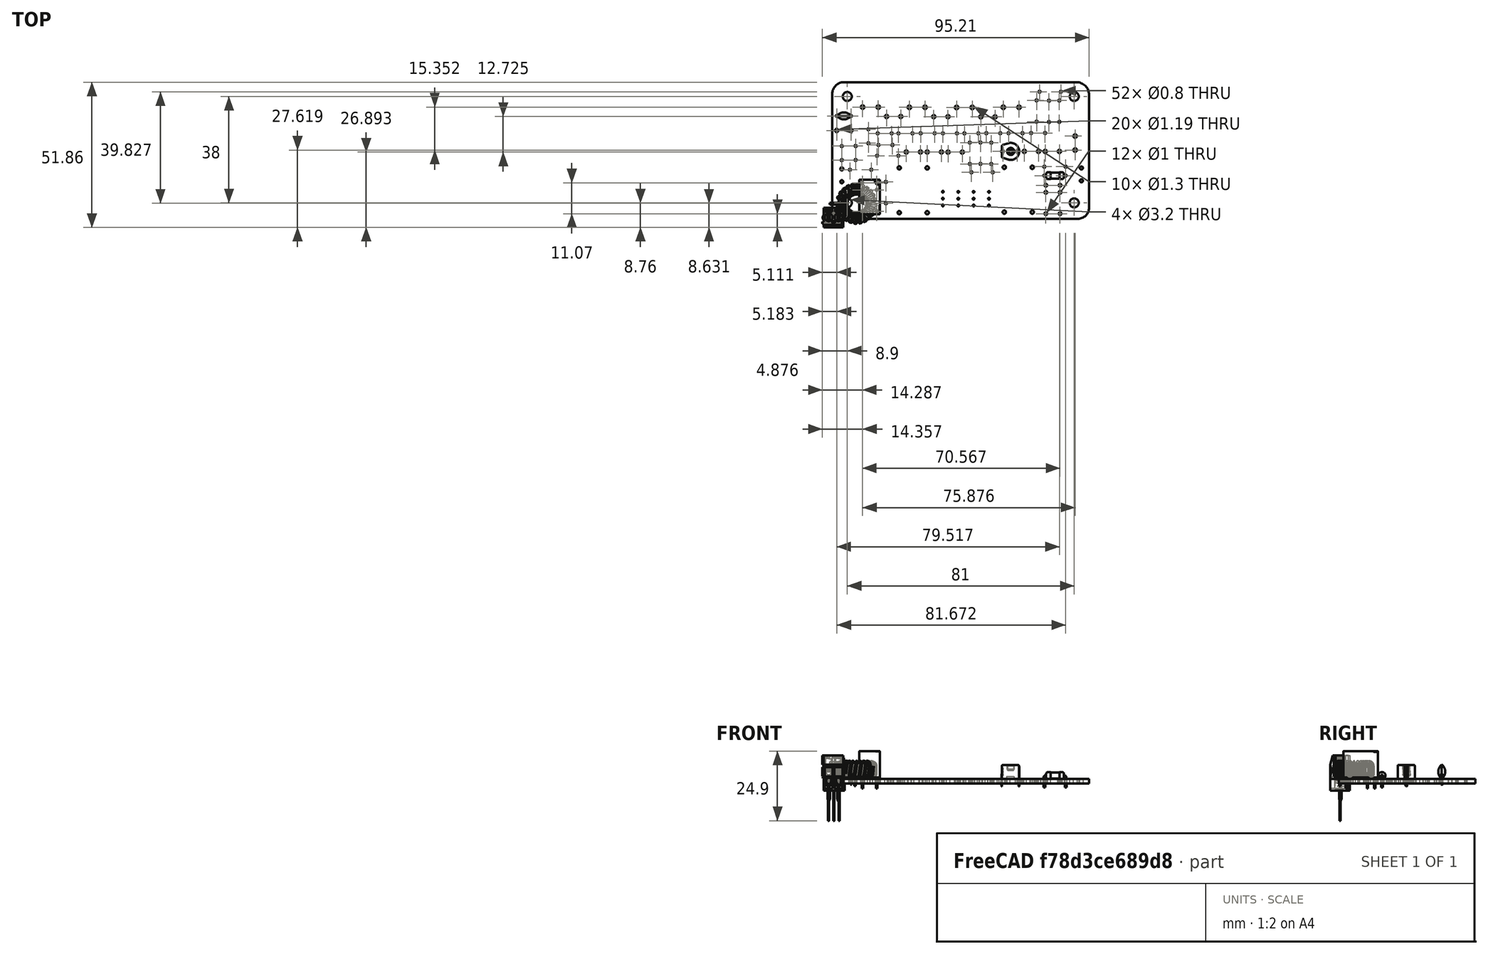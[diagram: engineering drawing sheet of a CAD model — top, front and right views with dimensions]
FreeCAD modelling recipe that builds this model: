
FCSTD DOCUMENT  (FreeCAD 0.19R24267 +148 (Git))
Label: resolution-filters
License: All rights reserved
LicenseURL: http://en.wikipedia.org/wiki/All_rights_reserved
objects: App::Link×60, Part::Feature×41, App::Part×10, PartDesign::CoordinateSystem×1, Sketcher::SketchObject×1
note: 43 computed .brp shape members not serialized (recipe doc carries the construction recipe); baked Part::Feature solids carry a one-line shape summary decoded from their .brp

FEATURE [PartDesign::CoordinateSystem] Local_CS_9a4e
  AttacherType = Attacher::AttachEngine3D
FEATURE [Part::Feature] Pcb_9a4e
  Placement = pos=(-101.6,111.76,0) rot=(0,0,1;0rad)
  shape: bbox 91.69 x 48.77 x 1.6 mm, 132 faces (baked)
FEATURE [Sketcher::SketchObject] PCB_Sketch_9a4e
  FullyConstrained = false
  sketch-geometry (8):
    g0: LineSegment StartX=86.7015 StartY=48.3617 StartZ=0 EndX=3.72385 EndY=48.3617 EndZ=0
    g1: LineSegment StartX=91.2113 StartY=3.58242 StartZ=0 EndX=91.2113 EndY=43.852 EndZ=0
    g2: LineSegment StartX=-0.482737 StartY=44.1551 StartZ=0 EndX=-0.482737 EndY=4.1461 EndZ=0
    g3: LineSegment StartX=4.06962 StartY=-0.40626 StartZ=0 EndX=87.2226 EndY=-0.40626 EndZ=0
    g4: ArcOfCircle CenterX=3.72386 CenterY=44.1551 CenterZ=0 NormalX=0 NormalY=0 NormalZ=-1 AngleXU=2.45258e-06 Radius=4.2066 StartAngle=0 EndAngle=1.57079
    g5: ArcOfCircle CenterX=4.06966 CenterY=4.14614 CenterZ=0 NormalX=0 NormalY=0 NormalZ=-1 AngleXU=-1.57079 Radius=4.5524 StartAngle=0 EndAngle=1.57078
    g6: ArcOfCircle CenterX=87.2226 CenterY=3.58243 CenterZ=0 NormalX=0 NormalY=0 NormalZ=-1 AngleXU=-3.14159 Radius=3.98869 StartAngle=0 EndAngle=1.57079
    g7: ArcOfCircle CenterX=86.7014 CenterY=43.8519 CenterZ=0 NormalX=0 NormalY=0 NormalZ=-1 AngleXU=1.5708 Radius=4.50982 StartAngle=0 EndAngle=1.57078
  constraints (8):
    c: Coincident(g2,g5)
    c: Coincident(g2,g4)
    c: Coincident(g0,g4)
    c: Coincident(g3,g5)
    c: Coincident(g0,g7)
    c: Coincident(g3,g6)
    c: Coincident(g1,g6)
    c: Coincident(g1,g7)
FEATURE [Part::Feature] Shape  label="C513_Trimmer Cap - Brown_fa101f9de910"
  Placement = pos=(60.4359,23.6475,0) rot=(0,0,1;0rad)
  shape: bbox 6.858 x 6.618 x 7.625 mm, 264 faces (baked)
FEATURE [App::Link] C513_Trimmer_Cap___Brown_fa101f9de910_ln_  label="C513_Trimmer Cap - Brown_fa101f9de910[2]"
  LinkPlacement = pos=(60.4359,23.6475,0) rot=(0,0,1;0rad)
  LinkedObject = -> Shape
  Placement = pos=(60.4359,23.6475,0) rot=(0,0,1;0rad)
FEATURE [App::Link] C513_Trimmer_Cap___Brown_fa101f9de910_ln_001  label="C510_Trimmer Cap - Brown_b6d9ad9018ce"
  LinkPlacement = pos=(18.9169,36.1188,0) rot=(0,0,1;0rad)
  LinkedObject = -> Shape
  Placement = pos=(18.9169,36.1188,0) rot=(0,0,1;0rad)
FEATURE [App::Link] C513_Trimmer_Cap___Brown_fa101f9de910_ln_002  label="C510_Trimmer Cap - Brown_b6d9ad9018ce[2]"
  LinkPlacement = pos=(18.9169,36.1188,0) rot=(0,0,1;0rad)
  LinkedObject = -> Shape
  Placement = pos=(18.9169,36.1188,0) rot=(0,0,1;0rad)
FEATURE [Part::Feature] Part__Feature  label="T37-6 IND"
  Placement = pos=(0,-2.7,-0.5) rot=(1,0,0;1.5708rad)
  shape: bbox 10.32 x 3.252 x 10.32 mm, 8 faces, 0 solids (baked)
FEATURE [Part::Feature] Part__Feature001  label="T37-6 IND001"
  Placement = pos=(0,-2.7,-0.5) rot=(1,0,0;1.5708rad)
  shape: bbox 10.51 x 3.773 x 9.618 mm, 81 faces, 0 solids (baked)
FEATURE [Part::Feature] Part__Feature002  label="T37-6 IND002"
  Placement = pos=(0,-2.7,-0.5) rot=(1,0,0;1.5708rad)
  shape: bbox 2.23 x 4.584 x 1.894 mm, 1 faces, 0 solids (baked)
FEATURE [Part::Feature] Part__Feature003  label="T37-6 IND003"
  Placement = pos=(0,-2.7,-0.5) rot=(1,0,0;1.5708rad)
  shape: bbox 1.873 x 4.219 x 1.831 mm, 1 faces, 0 solids (baked)
FEATURE [App::Part] T37_6_IND004  label="L501_T37-6 IND004_9cd36dea0652"
  Group = -> [Part__Feature,Part__Feature001,Part__Feature002,Part__Feature003]
  Origin = -> Origin008
  Placement = pos=(15.9572,39.4716,0) rot=(0,0,-1;1.5708rad)
FEATURE [App::Link] L501_T37_6_IND004_9cd36dea0652_ln_  label="L501_T37-6 IND004_9cd36dea0652[2]"
  LinkPlacement = pos=(15.9572,39.4716,0) rot=(0,0,-1;1.5708rad)
  LinkedObject = -> T37_6_IND004
  Placement = pos=(15.9572,39.4716,0) rot=(0,0,-1;1.5708rad)
FEATURE [Part::Feature] Shape001  label="R509_R_Axial_DIN0207_L63mm_D25mm_P762mm_Horizontal_29629d9bf234"
  Placement = pos=(75.2348,14.986,0) rot=(0,0,1;0rad)
  shape: bbox 8.418 x 2.706 x 5.603 mm, 15 faces (baked)
FEATURE [App::Link] R509_R_Axial_DIN0207_L63mm_D25mm_P762mm_Horizontal_29629d9bf234_ln_  label="R501_R_Axial_DIN0207_L63mm_D25mm_P762mm_Horizontal_7b32fe088733"
  LinkPlacement = pos=(13.4366,17.0942,0) rot=(0,0,1;3.14159rad)
  LinkedObject = -> Shape001
  Placement = pos=(13.4366,17.0942,0) rot=(0,0,1;3.14159rad)
FEATURE [App::Link] C513_Trimmer_Cap___Brown_fa101f9de910_ln_003  label="C516_Trimmer Cap - Brown_1af99d41cc4e"
  LinkPlacement = pos=(68.0875,23.6475,0) rot=(0,0,1;0rad)
  LinkedObject = -> Shape
  Placement = pos=(68.0875,23.6475,0) rot=(0,0,1;0rad)
FEATURE [App::Link] C513_Trimmer_Cap___Brown_fa101f9de910_ln_004  label="C516_Trimmer Cap - Brown_1af99d41cc4e[2]"
  LinkPlacement = pos=(68.0875,23.6475,0) rot=(0,0,1;0rad)
  LinkedObject = -> Shape
  Placement = pos=(68.0875,23.6475,0) rot=(0,0,1;0rad)
FEATURE [App::Link] C513_Trimmer_Cap___Brown_fa101f9de910_ln_005  label="C508_Trimmer Cap - Brown_be8f6a1adee0"
  LinkPlacement = pos=(33.4203,23.4188,0) rot=(0,0,1;0rad)
  LinkedObject = -> Shape
  Placement = pos=(33.4203,23.4188,0) rot=(0,0,1;0rad)
FEATURE [App::Link] C513_Trimmer_Cap___Brown_fa101f9de910_ln_006  label="C508_Trimmer Cap - Brown_be8f6a1adee0[2]"
  LinkPlacement = pos=(33.4203,23.4188,0) rot=(0,0,1;0rad)
  LinkedObject = -> Shape
  Placement = pos=(33.4203,23.4188,0) rot=(0,0,1;0rad)
FEATURE [App::Link] R509_R_Axial_DIN0207_L63mm_D25mm_P762mm_Horizontal_29629d9bf234_ln_001  label="R504_R_Axial_DIN0207_L63mm_D25mm_P762mm_Horizontal_66a026bb1076"
  LinkPlacement = pos=(73.533,44.958,0) rot=(0,0,1;0rad)
  LinkedObject = -> Shape001
  Placement = pos=(73.533,44.958,0) rot=(0,0,1;0rad)
FEATURE [App::Link] L501_T37_6_IND004_9cd36dea0652_ln_001  label="L503_T37-6 IND004_f84a305ee8ab"
  LinkPlacement = pos=(43.9106,39.3446,0) rot=(0,0,1;1.5708rad)
  LinkedObject = -> T37_6_IND004
  Placement = pos=(43.9106,39.3446,0) rot=(0,0,1;1.5708rad)
FEATURE [App::Link] L501_T37_6_IND004_9cd36dea0652_ln_002  label="L503_T37-6 IND004_f84a305ee8ab[2]"
  LinkPlacement = pos=(43.9106,39.3446,0) rot=(0,0,1;1.5708rad)
  LinkedObject = -> T37_6_IND004
  Placement = pos=(43.9106,39.3446,0) rot=(0,0,1;1.5708rad)
FEATURE [Part::Feature] Shape002  label="C506_C_Disc_D50mm_W25mm_P500mm_f2b36a464e24"
  Placement = pos=(1.183,36.322,0) rot=(0,0,1;0rad)
  shape: bbox 5.5 x 2.5 x 7.1 mm, 10 faces (baked)
FEATURE [App::Link] C513_Trimmer_Cap___Brown_fa101f9de910_ln_007  label="C520_Trimmer Cap - Brown_a66b8da15489"
  LinkPlacement = pos=(52.5719,35.9918,0) rot=(0,0,1;0rad)
  LinkedObject = -> Shape
  Placement = pos=(52.5719,35.9918,0) rot=(0,0,1;0rad)
FEATURE [App::Link] C513_Trimmer_Cap___Brown_fa101f9de910_ln_008  label="C520_Trimmer Cap - Brown_a66b8da15489[2]"
  LinkPlacement = pos=(52.5719,35.9918,0) rot=(0,0,1;0rad)
  LinkedObject = -> Shape
  Placement = pos=(52.5719,35.9918,0) rot=(0,0,1;0rad)
FEATURE [App::Link] R509_R_Axial_DIN0207_L63mm_D25mm_P762mm_Horizontal_29629d9bf234_ln_002  label="R503_R_Axial_DIN0207_L63mm_D25mm_P762mm_Horizontal_265a809a3c5d"
  LinkPlacement = pos=(18.669,12.7508,0) rot=(0,0,-1;1.5708rad)
  LinkedObject = -> Shape001
  Placement = pos=(18.669,12.7508,0) rot=(0,0,-1;1.5708rad)
FEATURE [App::Link] C513_Trimmer_Cap___Brown_fa101f9de910_ln_009  label="C515_Trimmer Cap - Brown_f30af8ea2418"
  LinkPlacement = pos=(35.7571,36.0426,0) rot=(0,0,1;0rad)
  LinkedObject = -> Shape
  Placement = pos=(35.7571,36.0426,0) rot=(0,0,1;0rad)
FEATURE [App::Link] C513_Trimmer_Cap___Brown_fa101f9de910_ln_010  label="C515_Trimmer Cap - Brown_f30af8ea2418[2]"
  LinkPlacement = pos=(35.7571,36.0426,0) rot=(0,0,1;0rad)
  LinkedObject = -> Shape
  Placement = pos=(35.7571,36.0426,0) rot=(0,0,1;0rad)
FEATURE [App::Link] L501_T37_6_IND004_9cd36dea0652_ln_003  label="L502_T37-6 IND004_d7aca97a7b04"
  LinkPlacement = pos=(27.045,39.3954,0) rot=(0,0,1;1.5708rad)
  LinkedObject = -> T37_6_IND004
  Placement = pos=(27.045,39.3954,0) rot=(0,0,1;1.5708rad)
FEATURE [App::Link] L501_T37_6_IND004_9cd36dea0652_ln_004  label="L502_T37-6 IND004_d7aca97a7b04[2]"
  LinkPlacement = pos=(27.045,39.3954,0) rot=(0,0,1;1.5708rad)
  LinkedObject = -> T37_6_IND004
  Placement = pos=(27.045,39.3954,0) rot=(0,0,1;1.5708rad)
FEATURE [App::Link] C506_C_Disc_D50mm_W25mm_P500mm_f2b36a464e24_ln_  label="C524_C_Disc_D50mm_W25mm_P500mm_c3d2106afa5c"
  LinkPlacement = pos=(62.4478,30.1498,0) rot=(0,0,1;0rad)
  LinkedObject = -> Shape002
  Placement = pos=(62.4478,30.1498,0) rot=(0,0,1;0rad)
FEATURE [App::Link] C506_C_Disc_D50mm_W25mm_P500mm_f2b36a464e24_ln_001  label="C521_C_Disc_D50mm_W25mm_P500mm_ee262ac6dc63"
  LinkPlacement = pos=(75.5142,30.2006,0) rot=(0,0,1;3.14159rad)
  LinkedObject = -> Shape002
  Placement = pos=(75.5142,30.2006,0) rot=(0,0,1;3.14159rad)
FEATURE [Part::Feature] Part__Feature004  label="UM-1"
  Placement = pos=(0.1,2e-15,0.6) rot=(1,0,0;1.5708rad)
  shape: bbox 8 x 3.2 x 7.5 mm, 36 faces (baked)
FEATURE [Part::Feature] Part__Feature005  label="UM-002"
  Placement = pos=(0.1,2e-15,0.6) rot=(1,0,0;1.5708rad)
  shape: bbox 1.2 x 1.2 x 0.5 mm, 6 faces (baked)
FEATURE [Part::Feature] Part__Feature006  label="UM-003"
  Placement = pos=(0.1,2e-15,0.6) rot=(1,0,0;1.5708rad)
  shape: bbox 1.2 x 1.2 x 0.5 mm, 6 faces (baked)
FEATURE [Part::Feature] Part__Feature007  label="UM-004"
  Placement = pos=(0.1,2e-15,0.6) rot=(1,0,0;1.5708rad)
  shape: bbox 0.35 x 0.35 x 15.5 mm, 4 faces (baked)
FEATURE [Part::Feature] Part__Feature008  label="UM-005"
  Placement = pos=(0.1,2e-15,0.6) rot=(1,0,0;1.5708rad)
  shape: bbox 0.35 x 0.35 x 15.5 mm, 4 faces (baked)
FEATURE [Part::Feature] Part__Feature009  label="UM-006"
  Placement = pos=(0.1,2e-15,0.6) rot=(1,0,0;1.5708rad)
  shape: bbox 0.35 x 0.35 x 15.5 mm, 4 faces (baked)
FEATURE [App::Part] UM_007  label="Y503_UM-007_13096f2298e0"
  Group = -> [Part__Feature004,Part__Feature005,Part__Feature006,Part__Feature007,Part__Feature008,Part__Feature009]
  Origin = -> Origin009
  Placement = pos=(49.9872,6.7641,0) rot=(0,0,1;1.5708rad)
FEATURE [App::Link] Y503_UM_007_13096f2298e0_ln_  label="Y503_UM-007_13096f2298e0[2]"
  LinkPlacement = pos=(49.9872,6.7641,0) rot=(0,0,1;1.5708rad)
  LinkedObject = -> UM_007
  Placement = pos=(49.9872,6.7641,0) rot=(0,0,1;1.5708rad)
FEATURE [App::Link] R509_R_Axial_DIN0207_L63mm_D25mm_P762mm_Horizontal_29629d9bf234_ln_003  label="R511_R_Axial_DIN0207_L63mm_D25mm_P762mm_Horizontal_370c389b173b"
  LinkPlacement = pos=(49.1744,16.1798,0) rot=(0,0,1;0rad)
  LinkedObject = -> Shape001
  Placement = pos=(49.1744,16.1798,0) rot=(0,0,1;0rad)
FEATURE [App::Link] R509_R_Axial_DIN0207_L63mm_D25mm_P762mm_Horizontal_29629d9bf234_ln_004  label="R506_R_Axial_DIN0207_L63mm_D25mm_P762mm_Horizontal_386c48cb915c"
  LinkPlacement = pos=(48.641,26.797,0) rot=(0,0,-1;1.5708rad)
  LinkedObject = -> Shape001
  Placement = pos=(48.641,26.797,0) rot=(0,0,-1;1.5708rad)
FEATURE [App::Link] R509_R_Axial_DIN0207_L63mm_D25mm_P762mm_Horizontal_29629d9bf234_ln_005  label="R502_R_Axial_DIN0207_L63mm_D25mm_P762mm_Horizontal_210b6273bd98"
  LinkPlacement = pos=(15.5194,22.098,0) rot=(0,0,1;0rad)
  LinkedObject = -> Shape001
  Placement = pos=(15.5194,22.098,0) rot=(0,0,1;0rad)
FEATURE [App::Link] C506_C_Disc_D50mm_W25mm_P500mm_f2b36a464e24_ln_002  label="C522_C_Disc_D50mm_W25mm_P500mm_f3233de2541f"
  LinkPlacement = pos=(46.6998,30.099,0) rot=(0,0,1;0rad)
  LinkedObject = -> Shape002
  Placement = pos=(46.6998,30.099,0) rot=(0,0,1;0rad)
FEATURE [Part::Feature] Part__Feature010  label="L_Tor_13x8x5_3a_cp"
  shape: bbox 14.07 x 14.07 x 5 mm, 8 faces (baked)
FEATURE [Part::Feature] Part__Feature011  label="L_Tor_13x8x5_3a_cp001"
  shape: bbox 16.93 x 14.67 x 6.694 mm, 203 faces (baked)
FEATURE [App::Part] L_Tor_13x8x5_3a_cp  label="T501_L_Tor_13x8x5_3a_cp002_fb5841712b66"
  Group = -> [Part__Feature010,Part__Feature011]
  Origin = -> Origin010
  Placement = pos=(23.4188,17.7546,0) rot=(0,0,-1;1.5708rad)
FEATURE [App::Link] T501_L_Tor_13x8x5_3a_cp002_fb5841712b66_ln_  label="T501_L_Tor_13x8x5_3a_cp002_fb5841712b66[2]"
  LinkPlacement = pos=(23.4188,17.7546,0) rot=(0,0,-1;1.5708rad)
  LinkedObject = -> L_Tor_13x8x5_3a_cp
  Placement = pos=(23.4188,17.7546,0) rot=(0,0,-1;1.5708rad)
FEATURE [App::Link] C513_Trimmer_Cap___Brown_fa101f9de910_ln_011  label="C505_Trimmer Cap - Brown_67148adb1c4f"
  LinkPlacement = pos=(25.9527,23.4442,0) rot=(0,0,1;0rad)
  LinkedObject = -> Shape
  Placement = pos=(25.9527,23.4442,0) rot=(0,0,1;0rad)
FEATURE [App::Link] C513_Trimmer_Cap___Brown_fa101f9de910_ln_012  label="C505_Trimmer Cap - Brown_67148adb1c4f[2]"
  LinkPlacement = pos=(25.9527,23.4442,0) rot=(0,0,1;0rad)
  LinkedObject = -> Shape
  Placement = pos=(25.9527,23.4442,0) rot=(0,0,1;0rad)
FEATURE [App::Link] C506_C_Disc_D50mm_W25mm_P500mm_f2b36a464e24_ln_003  label="C509_C_Disc_D50mm_W25mm_P500mm_400302d33418"
  LinkPlacement = pos=(15.7518,30.0991,0) rot=(0,0,1;0rad)
  LinkedObject = -> Shape002
  Placement = pos=(15.7518,30.0991,0) rot=(0,0,1;0rad)
FEATURE [App::Link] C506_C_Disc_D50mm_W25mm_P500mm_f2b36a464e24_ln_004  label="C514_C_Disc_D50mm_W25mm_P500mm_138143d8e988"
  LinkPlacement = pos=(23.1587,30.0991,0) rot=(0,0,1;0rad)
  LinkedObject = -> Shape002
  Placement = pos=(23.1587,30.0991,0) rot=(0,0,1;0rad)
FEATURE [App::Link] C506_C_Disc_D50mm_W25mm_P500mm_f2b36a464e24_ln_005  label="C507_C_Disc_D50mm_W25mm_P500mm_249115c39c3e"
  LinkPlacement = pos=(12.4206,31.5576,0) rot=(0,0,-1;1.5708rad)
  LinkedObject = -> Shape002
  Placement = pos=(12.4206,31.5576,0) rot=(0,0,-1;1.5708rad)
FEATURE [App::Link] C506_C_Disc_D50mm_W25mm_P500mm_f2b36a464e24_ln_006  label="C512_C_Disc_D50mm_W25mm_P500mm_561b1da62fe1"
  LinkPlacement = pos=(16.0166,25.9334,0) rot=(0,0,1;0rad)
  LinkedObject = -> Shape002
  Placement = pos=(16.0166,25.9334,0) rot=(0,0,1;0rad)
FEATURE [App::Link] Y503_UM_007_13096f2298e0_ln_001  label="Y504_UM-007_ad74b97e0cd8"
  LinkPlacement = pos=(55.4736,6.7641,0) rot=(0,0,1;1.5708rad)
  LinkedObject = -> UM_007
  Placement = pos=(55.4736,6.7641,0) rot=(0,0,1;1.5708rad)
FEATURE [App::Link] Y503_UM_007_13096f2298e0_ln_002  label="Y504_UM-007_ad74b97e0cd8[2]"
  LinkPlacement = pos=(55.4736,6.7641,0) rot=(0,0,1;1.5708rad)
  LinkedObject = -> UM_007
  Placement = pos=(55.4736,6.7641,0) rot=(0,0,1;1.5708rad)
FEATURE [App::Link] C506_C_Disc_D50mm_W25mm_P500mm_f2b36a464e24_ln_007  label="C517_C_Disc_D50mm_W25mm_P500mm_4a230a44a26d"
  LinkPlacement = pos=(31.0934,30.1244,0) rot=(0,0,1;0rad)
  LinkedObject = -> Shape002
  Placement = pos=(31.0934,30.1244,0) rot=(0,0,1;0rad)
FEATURE [App::Link] R509_R_Axial_DIN0207_L63mm_D25mm_P762mm_Horizontal_29629d9bf234_ln_006  label="R507_R_Axial_DIN0207_L63mm_D25mm_P762mm_Horizontal_1a8086ba3037"
  LinkPlacement = pos=(56.2864,19.1516,0) rot=(0,0,1;1.5708rad)
  LinkedObject = -> Shape001
  Placement = pos=(56.2864,19.1516,0) rot=(0,0,1;1.5708rad)
FEATURE [App::Link] C506_C_Disc_D50mm_W25mm_P500mm_f2b36a464e24_ln_008  label="C501_C_Disc_D50mm_W25mm_P500mm_c7547f0456a5"
  LinkPlacement = pos=(7.874,25.574,0) rot=(0,0,-1;1.5708rad)
  LinkedObject = -> Shape002
  Placement = pos=(7.874,25.574,0) rot=(0,0,-1;1.5708rad)
FEATURE [App::Link] T501_L_Tor_13x8x5_3a_cp002_fb5841712b66_ln_001  label="T502_L_Tor_13x8x5_3a_cp002_44b5b7291388"
  LinkPlacement = pos=(70.9384,1.9568,0) rot=(0,0,1;1.5708rad)
  LinkedObject = -> L_Tor_13x8x5_3a_cp
  Placement = pos=(70.9384,1.9568,0) rot=(0,0,1;1.5708rad)
FEATURE [App::Link] T501_L_Tor_13x8x5_3a_cp002_fb5841712b66_ln_002  label="T502_L_Tor_13x8x5_3a_cp002_44b5b7291388[2]"
  LinkPlacement = pos=(70.9384,1.9568,0) rot=(0,0,1;1.5708rad)
  LinkedObject = -> L_Tor_13x8x5_3a_cp
  Placement = pos=(70.9384,1.9568,0) rot=(0,0,1;1.5708rad)
FEATURE [App::Link] Y503_UM_007_13096f2298e0_ln_003  label="Y501_UM-007_785145fc44e6"
  LinkPlacement = pos=(39.0144,6.7895,0) rot=(0,0,1;1.5708rad)
  LinkedObject = -> UM_007
  Placement = pos=(39.0144,6.7895,0) rot=(0,0,1;1.5708rad)
FEATURE [App::Link] Y503_UM_007_13096f2298e0_ln_004  label="Y501_UM-007_785145fc44e6[2]"
  LinkPlacement = pos=(39.0144,6.7895,0) rot=(0,0,1;1.5708rad)
  LinkedObject = -> UM_007
  Placement = pos=(39.0144,6.7895,0) rot=(0,0,1;1.5708rad)
FEATURE [App::Link] R509_R_Axial_DIN0207_L63mm_D25mm_P762mm_Horizontal_29629d9bf234_ln_007  label="R510_R_Axial_DIN0207_L63mm_D25mm_P762mm_Horizontal_af9739584a69"
  LinkPlacement = pos=(75.2348,18.1864,0) rot=(0,0,1;0rad)
  LinkedObject = -> Shape001
  Placement = pos=(75.2348,18.1864,0) rot=(0,0,1;0rad)
FEATURE [App::Link] C506_C_Disc_D50mm_W25mm_P500mm_f2b36a464e24_ln_009  label="C523_C_Disc_D50mm_W25mm_P500mm_b693a0d0fd5f"
  LinkPlacement = pos=(54.5122,30.1498,0) rot=(0,0,1;0rad)
  LinkedObject = -> Shape002
  Placement = pos=(54.5122,30.1498,0) rot=(0,0,1;0rad)
FEATURE [App::Link] C506_C_Disc_D50mm_W25mm_P500mm_f2b36a464e24_ln_010  label="C519_C_Disc_D50mm_W25mm_P500mm_4a3058133605"
  LinkPlacement = pos=(39.0337,30.0991,0) rot=(0,0,1;0rad)
  LinkedObject = -> Shape002
  Placement = pos=(39.0337,30.0991,0) rot=(0,0,1;0rad)
FEATURE [Part::Feature] Part__Feature012  label="D_DO-35_SOD27_P7.62mm_Horizontal"
  shape: bbox 8.244 x 0.5 x 4.312 mm, 7 faces (baked)
FEATURE [Part::Feature] Part__Feature013  label="D_DO-35_SOD27_P7.62mm_Horizontal001"
  shape: bbox 4 x 2.165 x 2.165 mm, 9 faces (baked)
FEATURE [App::Part] D_DO_35_SOD27_P7_62mm_Horizontal  label="D501_D_DO-35_SOD27_P7.62mm_Horizontal002_73c7e2338286"
  Group = -> [Part__Feature012,Part__Feature013]
  Origin = -> Origin011
  Placement = pos=(72.4916,41.8846,0) rot=(0,0,-1;1.5708rad)
FEATURE [Part::Feature] Shape003  label="K501_Relay_SPDT_Omron_G5V-1_adee48805411"
  Placement = pos=(10.287,12.446,0) rot=(0,0,1;0rad)
  shape: bbox 7.3 x 12.3 x 13.4 mm, 63 faces (baked)
FEATURE [App::Link] C513_Trimmer_Cap___Brown_fa101f9de910_ln_013  label="C511_Trimmer Cap - Brown_927071e8bfa3"
  LinkPlacement = pos=(40.8686,23.3934,0) rot=(0,0,1;0rad)
  LinkedObject = -> Shape
  Placement = pos=(40.8686,23.3934,0) rot=(0,0,1;0rad)
FEATURE [App::Link] C513_Trimmer_Cap___Brown_fa101f9de910_ln_014  label="C511_Trimmer Cap - Brown_927071e8bfa3[2]"
  LinkPlacement = pos=(40.8686,23.3934,0) rot=(0,0,1;0rad)
  LinkedObject = -> Shape
  Placement = pos=(40.8686,23.3934,0) rot=(0,0,1;0rad)
FEATURE [App::Link] R509_R_Axial_DIN0207_L63mm_D25mm_P762mm_Horizontal_29629d9bf234_ln_008  label="R505_R_Axial_DIN0207_L63mm_D25mm_P762mm_Horizontal_e8e929966ea1"
  LinkPlacement = pos=(52.451,19.2024,0) rot=(0,0,1;1.5708rad)
  LinkedObject = -> Shape001
  Placement = pos=(52.451,19.2024,0) rot=(0,0,1;1.5708rad)
FEATURE [App::Link] L501_T37_6_IND004_9cd36dea0652_ln_005  label="L504_T37-6 IND004_e213a2609321"
  LinkPlacement = pos=(60.5984,39.3954,0) rot=(0,0,1;1.5708rad)
  LinkedObject = -> T37_6_IND004
  Placement = pos=(60.5984,39.3954,0) rot=(0,0,1;1.5708rad)
FEATURE [App::Link] L501_T37_6_IND004_9cd36dea0652_ln_006  label="L504_T37-6 IND004_e213a2609321[2]"
  LinkPlacement = pos=(60.5984,39.3954,0) rot=(0,0,1;1.5708rad)
  LinkedObject = -> T37_6_IND004
  Placement = pos=(60.5984,39.3954,0) rot=(0,0,1;1.5708rad)
FEATURE [App::Link] C513_Trimmer_Cap___Brown_fa101f9de910_ln_015  label="C518_Trimmer Cap - Brown_428f74104fa1"
  LinkPlacement = pos=(75.5489,23.6475,0) rot=(0,0,1;0rad)
  LinkedObject = -> Shape
  Placement = pos=(75.5489,23.6475,0) rot=(0,0,1;0rad)
FEATURE [App::Link] C513_Trimmer_Cap___Brown_fa101f9de910_ln_016  label="C518_Trimmer Cap - Brown_428f74104fa1[2]"
  LinkPlacement = pos=(75.5489,23.6475,0) rot=(0,0,1;0rad)
  LinkedObject = -> Shape
  Placement = pos=(75.5489,23.6475,0) rot=(0,0,1;0rad)
FEATURE [App::Link] R509_R_Axial_DIN0207_L63mm_D25mm_P762mm_Horizontal_29629d9bf234_ln_009  label="R508_R_Axial_DIN0207_L63mm_D25mm_P762mm_Horizontal_3ea6de62e5e0"
  LinkPlacement = pos=(80.5942,41.8084,0) rot=(0,0,-1;1.5708rad)
  LinkedObject = -> Shape001
  Placement = pos=(80.5942,41.8084,0) rot=(0,0,-1;1.5708rad)
FEATURE [Part::Feature] Part__Feature014  label="SOLID"
  shape: bbox 8 x 7 x 8.4 mm, 72 faces (baked)
FEATURE [Part::Feature] Part__Feature015  label="SOLID001"
  shape: bbox 2.75 x 3.75 x 8.15 mm, 17 faces (baked)
FEATURE [Part::Feature] Part__Feature016  label="SOLID002"
  shape: bbox 2.75 x 3.75 x 8.15 mm, 17 faces (baked)
FEATURE [Part::Feature] Part__Feature017  label="SOLID003"
  shape: bbox 2.9 x 4.5 x 2.65 mm, 46 faces (baked)
FEATURE [Part::Feature] Part__Feature018  label="SOLID004"
  shape: bbox 2.9 x 4.5 x 2.65 mm, 46 faces (baked)
FEATURE [Part::Feature] Part__Feature019  label="SOLID005"
  shape: bbox 3.139 x 3.139 x 4.6 mm, 17 faces (baked)
FEATURE [Part::Feature] Part__Feature020  label="SOLID006"
  shape: bbox 3.139 x 3.139 x 4.6 mm, 17 faces (baked)
FEATURE [App::Part] _91103110002_1  label="J502_691103110002_1_665a677e1f96"
  Group = -> [Part__Feature014,Part__Feature015,Part__Feature016,Part__Feature017,Part__Feature018,Part__Feature019,Part__Feature020]
  Origin = -> Origin012
  Placement = pos=(86.233,26.6192,0) rot=(0,0,1;1.5708rad)
FEATURE [Part::Feature] Part__Feature021  label="SOLID007"
  Placement = pos=(0,0,4.2) rot=(0,0,1;0rad)
  shape: bbox 8 x 7 x 8.4 mm, 72 faces (baked)
FEATURE [Part::Feature] Part__Feature022  label="SOLID008"
  Placement = pos=(0,0,4.2) rot=(0,0,1;0rad)
  shape: bbox 2.75 x 3.75 x 8.15 mm, 17 faces (baked)
FEATURE [Part::Feature] Part__Feature023  label="SOLID009"
  Placement = pos=(0,0,4.2) rot=(0,0,1;0rad)
  shape: bbox 2.75 x 3.75 x 8.15 mm, 17 faces (baked)
FEATURE [Part::Feature] Part__Feature024  label="SOLID010"
  Placement = pos=(0,0,4.2) rot=(0,0,1;0rad)
  shape: bbox 2.9 x 4.5 x 2.65 mm, 46 faces (baked)
FEATURE [Part::Feature] Part__Feature025  label="SOLID011"
  Placement = pos=(0,0,4.2) rot=(0,0,1;0rad)
  shape: bbox 2.9 x 4.5 x 2.65 mm, 46 faces (baked)
FEATURE [Part::Feature] Part__Feature026  label="SOLID012"
  Placement = pos=(0,0,4.2) rot=(0,0,1;0rad)
  shape: bbox 3.139 x 3.139 x 4.6 mm, 17 faces (baked)
FEATURE [Part::Feature] Part__Feature027  label="SOLID013"
  Placement = pos=(0,0,4.2) rot=(0,0,1;0rad)
  shape: bbox 3.139 x 3.139 x 4.6 mm, 17 faces (baked)
FEATURE [App::Part] _91103110002_1001  label="J502_691103110002_1_665a677e1f96[2]"
  Group = -> [Part__Feature021,Part__Feature022,Part__Feature023,Part__Feature024,Part__Feature025,Part__Feature026,Part__Feature027]
  Origin = -> Origin013
  Placement = pos=(86.233,26.6192,0) rot=(0,0,1;1.5708rad)
FEATURE [App::Link] D501_D_DO_35_SOD27_P7_62mm_Horizontal002_73c7e2338286_ln_  label="D502_D_DO-35_SOD27_P7.62mm_Horizontal002_b64abd241756"
  LinkPlacement = pos=(76.9112,34.1376,0) rot=(0,0,1;1.5708rad)
  LinkedObject = -> D_DO_35_SOD27_P7_62mm_Horizontal
  Placement = pos=(76.9112,34.1376,0) rot=(0,0,1;1.5708rad)
FEATURE [App::Link] C506_C_Disc_D50mm_W25mm_P500mm_f2b36a464e24_ln_011  label="C502_C_Disc_D50mm_W25mm_P500mm_6ff8c0575432"
  LinkPlacement = pos=(2.921,20.534,0) rot=(0,0,1;1.5708rad)
  LinkedObject = -> Shape002
  Placement = pos=(2.921,20.534,0) rot=(0,0,1;1.5708rad)
FEATURE [App::Link] C513_Trimmer_Cap___Brown_fa101f9de910_ln_017  label="C504_Trimmer Cap - Brown_60e580f9c6ba"
  LinkPlacement = pos=(1.1115,31.115,0) rot=(0,0,1;0rad)
  LinkedObject = -> Shape
  Placement = pos=(1.1115,31.115,0) rot=(0,0,1;0rad)
FEATURE [App::Link] C513_Trimmer_Cap___Brown_fa101f9de910_ln_018  label="C504_Trimmer Cap - Brown_60e580f9c6ba[2]"
  LinkPlacement = pos=(1.1115,31.115,0) rot=(0,0,1;0rad)
  LinkedObject = -> Shape
  Placement = pos=(1.1115,31.115,0) rot=(0,0,1;0rad)
FEATURE [App::Link] K501_Relay_SPDT_Omron_G5V_1_adee48805411_ln_  label="K502_Relay_SPDT_Omron_G5V-1_3b78f154928e"
  LinkPlacement = pos=(75.7737,11.5361,0) rot=(0,0,1;0rad)
  LinkedObject = -> Shape003
  Placement = pos=(75.7737,11.5361,0) rot=(0,0,1;0rad)
FEATURE [App::Link] Y503_UM_007_13096f2298e0_ln_005  label="Y502_UM-007_56b8e91b9b57"
  LinkPlacement = pos=(44.5262,6.7642,0) rot=(0,0,1;1.5708rad)
  LinkedObject = -> UM_007
  Placement = pos=(44.5262,6.7642,0) rot=(0,0,1;1.5708rad)
FEATURE [App::Link] Y503_UM_007_13096f2298e0_ln_006  label="Y502_UM-007_56b8e91b9b57[2]"
  LinkPlacement = pos=(44.5262,6.7642,0) rot=(0,0,1;1.5708rad)
  LinkedObject = -> UM_007
  Placement = pos=(44.5262,6.7642,0) rot=(0,0,1;1.5708rad)
FEATURE [App::Part] Top_9a4e
  Group = -> [Shape,C513_Trimmer_Cap___Brown_fa101f9de910_ln_,C513_Trimmer_Cap___Brown_fa101f9de910_ln_001,C513_Trimmer_Cap___Brown_fa101f9de910_ln_002,T37_6_IND004,L501_T37_6_IND004_9cd36dea0652_ln_,Shape001,R509_R_Axial_DIN0207_L63mm_D25mm_P762mm_Horizontal_29629d9bf234_ln_,C513_Trimmer_Cap___Brown_fa101f9de910_ln_003,C513_Trimmer_Cap___Brown_fa101f9de910_ln_004,C513_Trimmer_Cap___Brown_fa101f9de910_ln_005,+59 more]
  Origin = -> Origin003
FEATURE [App::Part] Step_Models_9a4e
  Group = -> [Top_9a4e]
  Origin = -> Origin002
FEATURE [Part::Feature] pads_area061001  label="topPads_9a4e"
  Placement = pos=(-101.6,111.76,0.02) rot=(0,0,1;0rad)
  shape: bbox 89.26 x 45.5 x 2e-07 mm, 124 faces, 0 solids (baked)
FEATURE [Part::Feature] Shape004001  label="topTracks_9a4e"
  Placement = pos=(-101.6,111.76,0.01) rot=(0,0,1;0rad)
  shape: bbox 82.77 x 43.33 x 2e-07 mm, 39 faces, 0 solids (baked)
FEATURE [Part::Feature] zones_area001  label="topZones_9a4e"
  Placement = pos=(-101.6,111.76,0.01) rot=(0,0,1;0rad)
  shape: bbox 90.93 x 48.01 x 2e-07 mm, 4 faces, 0 solids (baked)
FEATURE [Part::Feature] pads_area061057001  label="botPads_9a4e"
  Placement = pos=(-101.6,111.76,-1.62) rot=(0,0,1;0rad)
  shape: bbox 89.26 x 45.5 x 2e-07 mm, 118 faces, 0 solids (baked)
FEATURE [Part::Feature] Shape004002001  label="botTracks_9a4e"
  Placement = pos=(-101.6,111.76,-1.61) rot=(0,0,1;0rad)
  shape: bbox 88.37 x 42.72 x 2e-07 mm, 43 faces, 0 solids (baked)
FEATURE [Part::Feature] zones_area002001  label="botZones_9a4e"
  Placement = pos=(-101.6,111.76,-1.61) rot=(0,0,1;0rad)
  shape: bbox 90.93 x 48.01 x 2e-07 mm, 4 faces, 0 solids (baked)
FEATURE [Part::Feature] botSilks_1b10
  Placement = pos=(-101.6,111.76,-1.67) rot=(0,0,1;0rad)
  shape: bbox 58.78 x 4.817 x 2e-07 mm, 70 faces, 0 solids (baked)
FEATURE [Part::Feature] topSilks_16c4
  Placement = pos=(-101.6,111.76,0.07) rot=(0,0,1;0rad)
  shape: bbox 90.39 x 46.31 x 2e-07 mm, 414 faces, 0 solids (baked)
FEATURE [App::Part] Board_Geoms_9a4e
  Group = -> [Local_CS_9a4e,Pcb_9a4e,PCB_Sketch_9a4e,pads_area061001,Shape004001,zones_area001,pads_area061057001,Shape004002001,zones_area002001,botSilks_1b10,topSilks_16c4]
  Origin = -> Origin
FEATURE [App::Part] Board_9a4e  label="resolution-filters"
  Group = -> [Board_Geoms_9a4e,Step_Models_9a4e]
  Origin = -> Origin001
